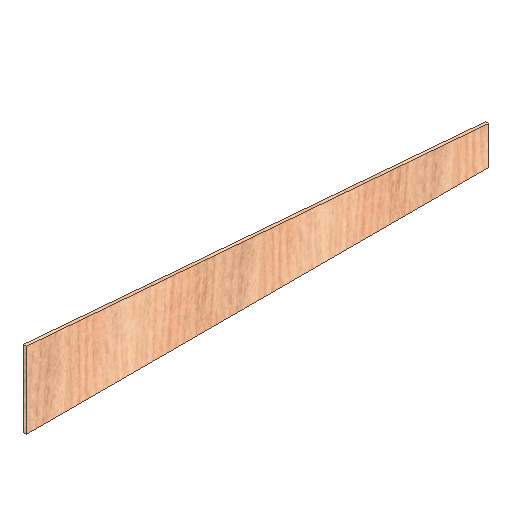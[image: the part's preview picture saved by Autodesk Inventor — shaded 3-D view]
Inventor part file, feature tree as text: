
AUTODESK INVENTOR PART (.ipt)
format: ipt  version: 2021 (Build 250183000, 183)  size: 160,256 bytes
history: native  units: mm
features: extrude x1, sketch x1
ambient origin geometry x8: Origin, YZ Plane, XZ Plane, XY Plane, X Axis, Y Axis, Z Axis, Center Point
bodies: Solid1 (feature_tree)
feature tree (2):
  extrude  "Extrusion1"  Depth=605.88mm
  sketch  "Sketch1"  dims[d2=4.0mm d3=0.0mm d4=100.0mm d6=605.88mm d7=50.0mm]
